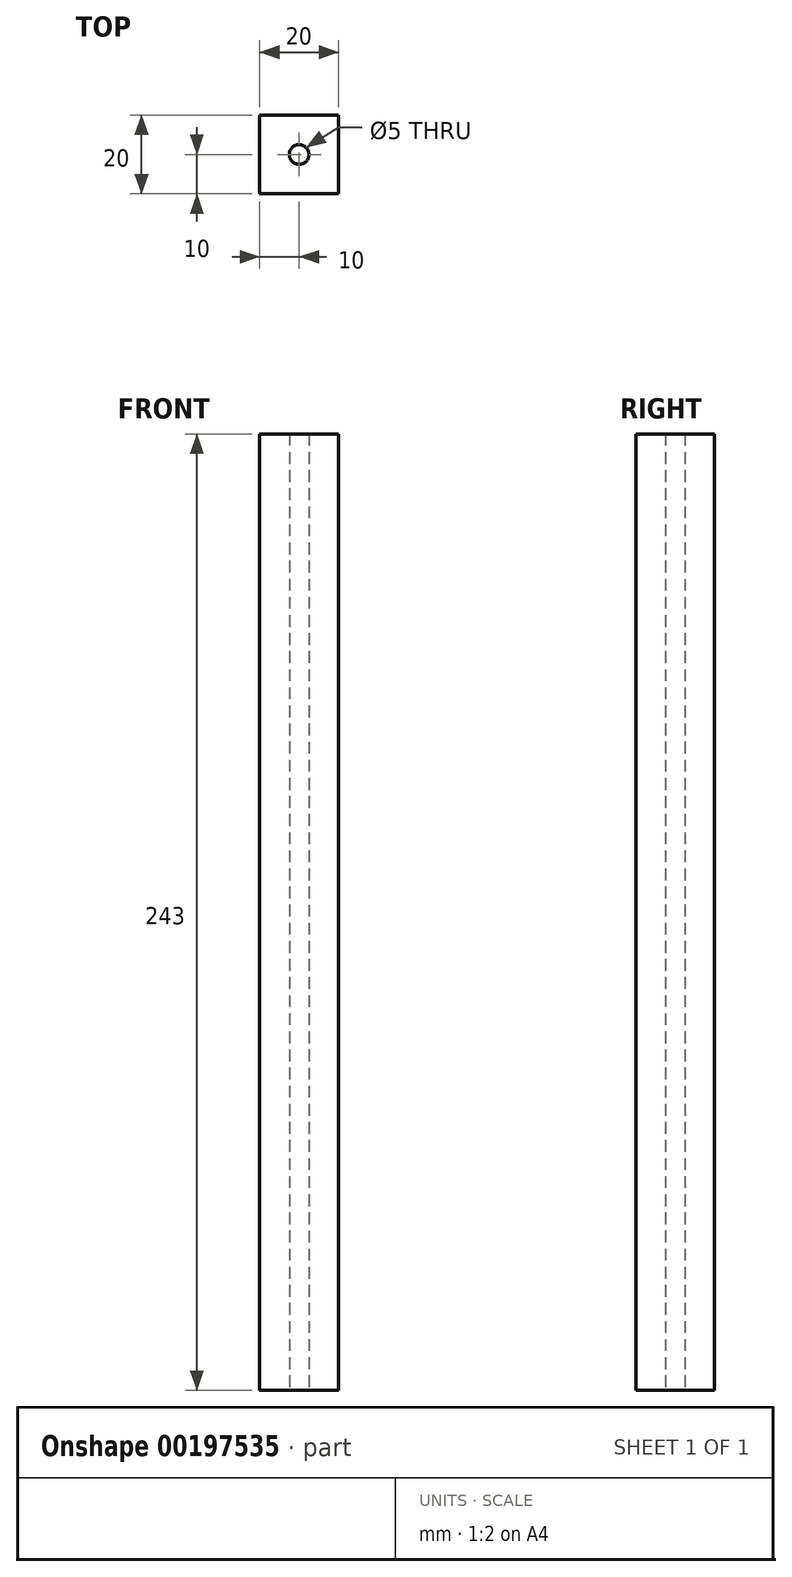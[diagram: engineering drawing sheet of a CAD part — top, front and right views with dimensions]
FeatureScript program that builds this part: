
annotation { "Feature Type Name" : "Feature", "Feature Type Description" : "" }
export const myFeature = defineFeature(function(context is Context, id is Id, definition is map)
    precondition{}
    {
        {
            var Q0;
            Q0=qCreatedBy(makeId("Top.planeOp"),FACE);
            var sketch = newSketch(context, id + "F0", { "sketchPlane" : qUnion([Q0])});
            skLineSegment(sketch, "E0.bottom", {"start": v(-10, 10) * mm, "end": v(10, 10) * mm});
            skLineSegment(sketch, "E0.top", {"start": v(-10, -10) * mm, "end": v(10, -10) * mm});
            skLineSegment(sketch, "E0.left", {"start": v(-10, 10) * mm, "end": v(-10, -10) * mm});
            skLineSegment(sketch, "E0.right", {"start": v(10, 10) * mm, "end": v(10, -10) * mm});
            skCircle(sketch, "E1", {"center": v(0, 0) * mm, "radius": 2.5 * mm});
            skSolve(sketch);
        }
        {
            var Q0;
            Q0=qSketchRegion(id+"F0",true);
            extrude(context, id + "F1", {"entities" : qUnion([Q0]), "depth" : 243 * mm});
        }
        {
            var Q0;
            Q0=makeQuery(id+"F1.opExtrude","SWEPT_FACE",FACE,{"disambiguationData":[OSD([sQuery(id+"F0.wireOp",EDGE,"E0.right")])]});
            var sketch = newSketch(context, id + "F2", { "sketchPlane" : qUnion([Q0])});
            skCircle(sketch, "E2", {"center": v(0, 10) * mm, "radius": 2.5 * mm});
            skSolve(sketch);
        }
    });
